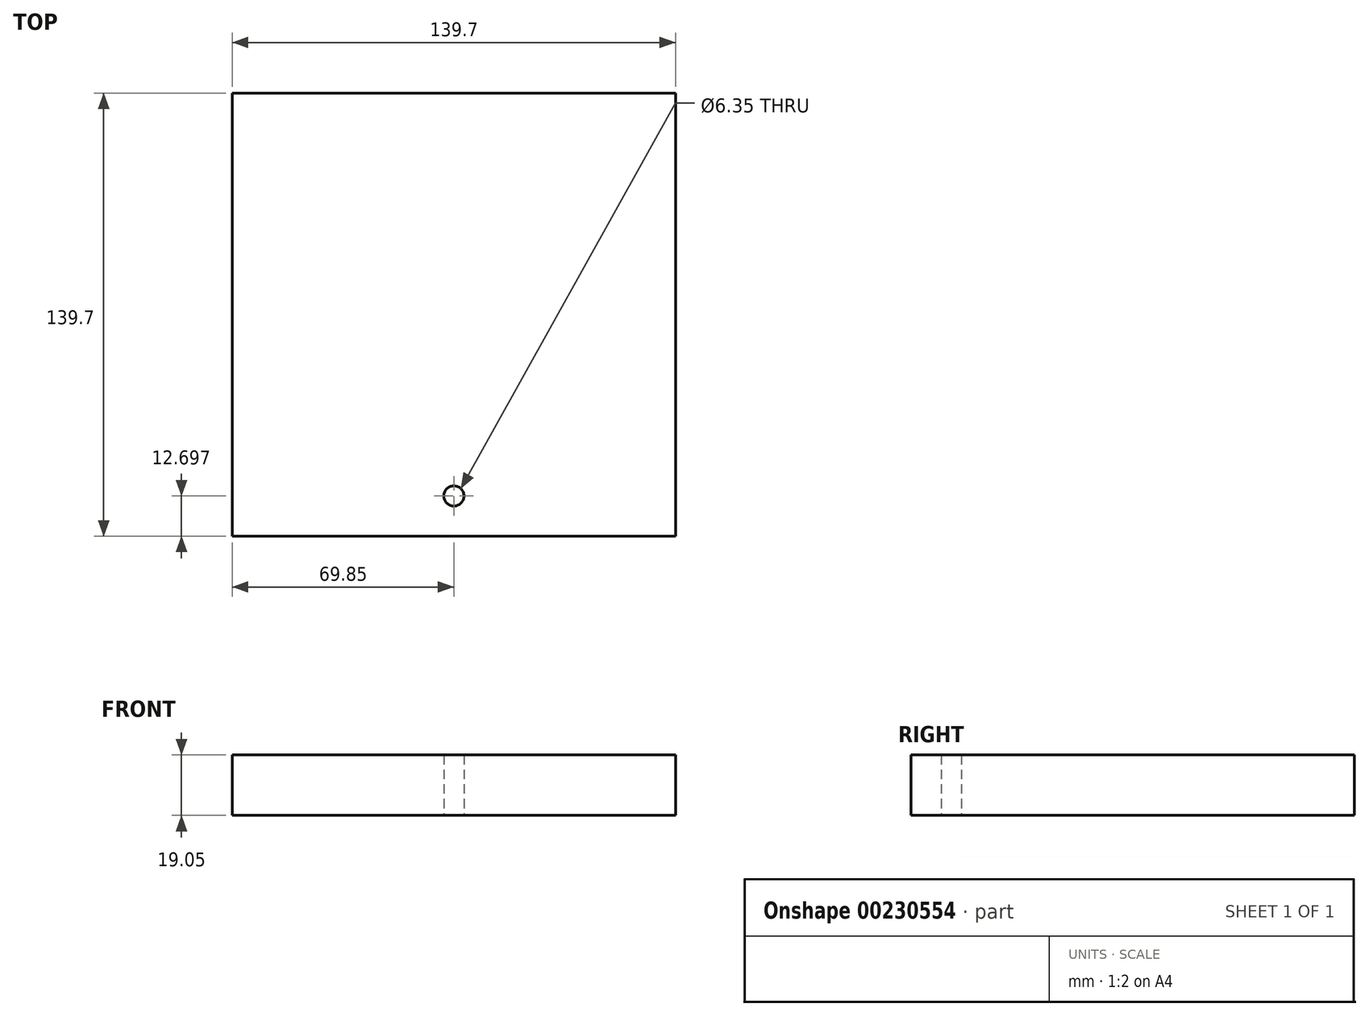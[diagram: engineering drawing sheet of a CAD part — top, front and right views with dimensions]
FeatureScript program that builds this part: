
annotation { "Feature Type Name" : "Feature", "Feature Type Description" : "" }
export const myFeature = defineFeature(function(context is Context, id is Id, definition is map)
    precondition{}
    {
        {
            var Q0;
            Q0=qCreatedBy(makeId("Top.planeOp"),FACE);
            var sketch = newSketch(context, id + "F0", { "sketchPlane" : qUnion([Q0])});
            skLineSegment(sketch, "E0.bottom", {"start": v(-69.85, 72.56) * mm, "end": v(69.85, 72.56) * mm});
            skLineSegment(sketch, "E0.top", {"start": v(-69.85, -67.14) * mm, "end": v(69.85, -67.14) * mm});
            skLineSegment(sketch, "E0.left", {"start": v(-69.85, 72.56) * mm, "end": v(-69.85, -67.14) * mm});
            skLineSegment(sketch, "E0.right", {"start": v(69.85, 72.56) * mm, "end": v(69.85, -67.14) * mm});
            skPoint(sketch, "E0.middle", {"position": v(0, 2.7) * mm});
            skLineSegment(sketch, "E1", {"start": v(0, -67.14) * mm, "end": v(0, -54.44) * mm});
            skPoint(sketch, "E1.endSnap0", {"position": v(0, -67.14) * mm});
            skCircle(sketch, "E2", {"center": v(0, -54.44) * mm, "radius": 3.18 * mm});
            skSolve(sketch);
        }
        {
            var Q0;
            Q0 = qSketchRegion(id + "F0", true);
            extrude(context, id + "F1", {"entities" : qUnion([Q0]), "depth" : 19.05 * mm});
        }
    });
